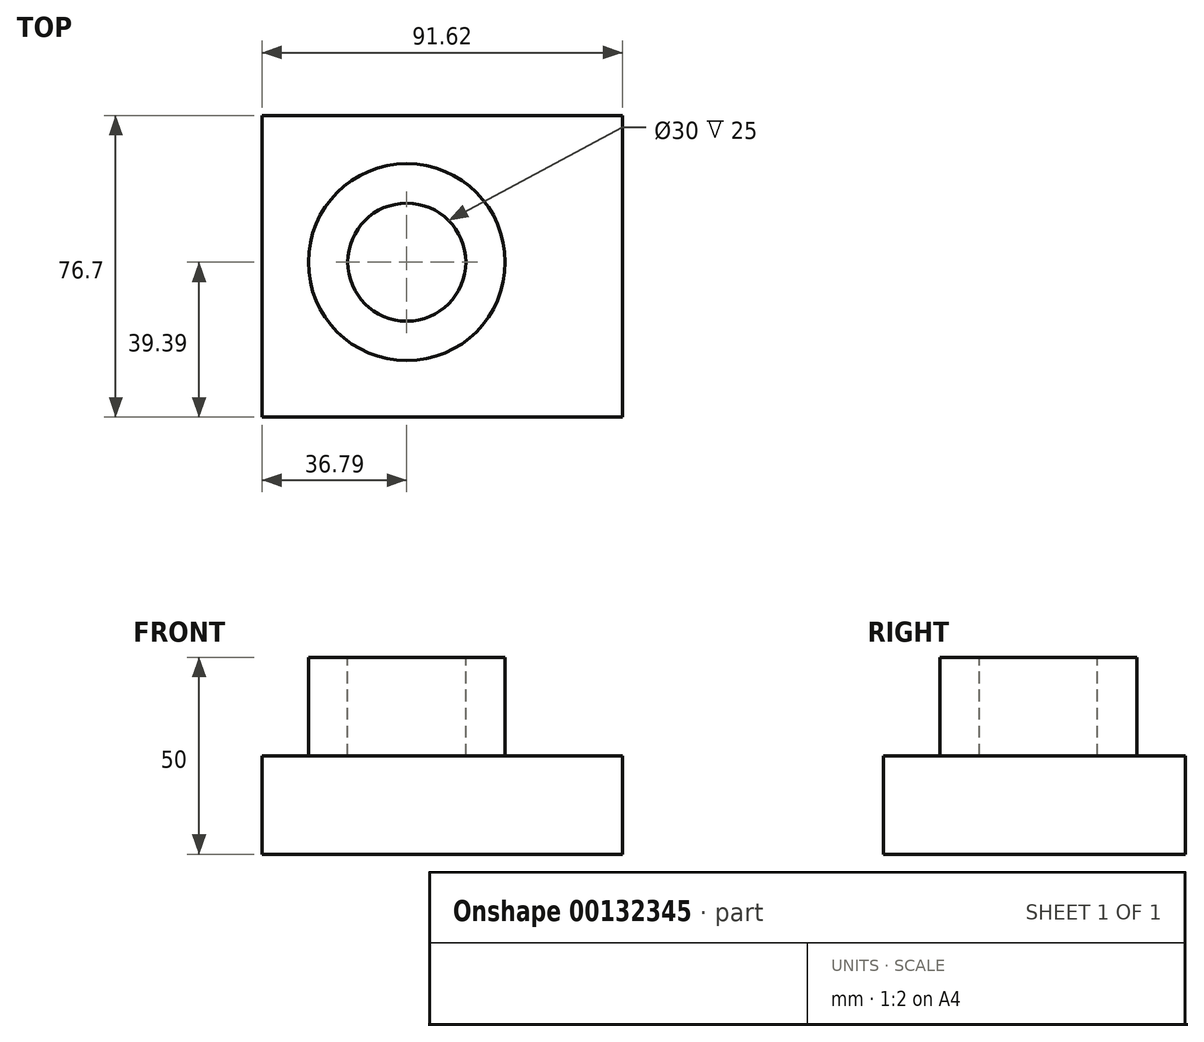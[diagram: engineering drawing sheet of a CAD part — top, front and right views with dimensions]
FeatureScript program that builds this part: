
annotation { "Feature Type Name" : "Feature", "Feature Type Description" : "" }
export const myFeature = defineFeature(function(context is Context, id is Id, definition is map)
    precondition{}
    {
        {
            var Q0;
            Q0=qCreatedBy(makeId("Top.planeOp"),FACE);
            var sketch = newSketch(context, id + "F0", { "sketchPlane" : qUnion([Q0])});
            skCircle(sketch, "E0", {"center": v(0, 0) * mm, "radius": 25 * mm});
            skSolve(sketch);
        }
        {
            var Q0;
            Q0=qSketchRegion(id+"F0",true);
            extrude(context, id + "F1", {"entities" : qUnion([Q0]), "depth" : 50 * mm});
        }
        {
            var Q0;
            Q0=makeQuery(id+"F1.opExtrude","CAP_FACE",FACE,{"disambiguationData":[OSD([sQuery(id+"F0.wireOp",EDGE,"E0")])],"isStart":false});
            var sketch = newSketch(context, id + "F2", { "sketchPlane" : qUnion([Q0])});
            skCircle(sketch, "E1", {"center": v(0, 0) * mm, "radius": 15 * mm});
            skSolve(sketch);
        }
        {
            var Q0;
            Q0=qSketchRegion(id+"F2",true);
            extrude(context, id + "F3", {"entities" : qUnion([Q0]), "operationType" : NewBodyOperationType.REMOVE, "endBound" : BoundingType.THROUGH_ALL, "oppositeDirection" : true, "depth" : 25 * mm});
        }
        {
            var Q0;
            Q0=qCreatedBy(makeId("Top.planeOp"),FACE);
            var sketch = newSketch(context, id + "F4", { "sketchPlane" : qUnion([Q0])});
            skLineSegment(sketch, "E2.bottom", {"start": v(-36.79, 37.3) * mm, "end": v(54.83, 37.3) * mm});
            skLineSegment(sketch, "E2.top", {"start": v(-36.79, -39.39) * mm, "end": v(54.83, -39.39) * mm});
            skLineSegment(sketch, "E2.left", {"start": v(-36.79, 37.3) * mm, "end": v(-36.79, -39.39) * mm});
            skLineSegment(sketch, "E2.right", {"start": v(54.83, 37.3) * mm, "end": v(54.83, -39.39) * mm});
            skSolve(sketch);
        }
        {
            var Q0;
            Q0=qSketchRegion(id+"F4",true);
            extrude(context, id + "F5", {"entities" : qUnion([Q0]), "operationType" : NewBodyOperationType.ADD, "depth" : 25 * mm});
        }
    });
